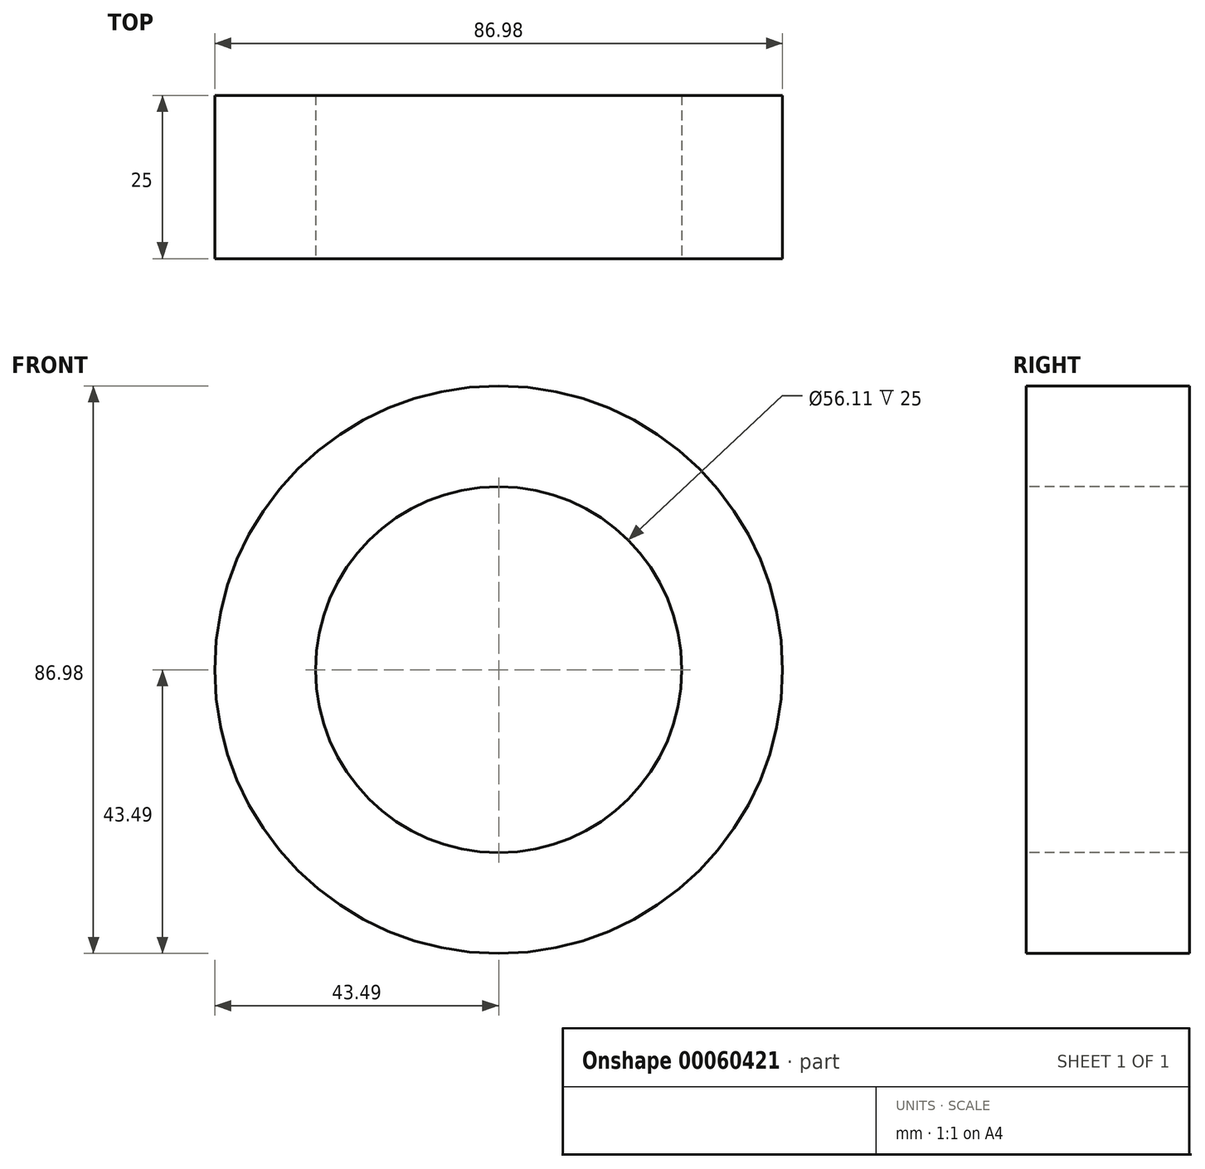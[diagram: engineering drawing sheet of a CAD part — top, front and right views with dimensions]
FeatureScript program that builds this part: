
annotation { "Feature Type Name" : "Feature", "Feature Type Description" : "" }
export const myFeature = defineFeature(function(context is Context, id is Id, definition is map)
    precondition{}
    {
        {
            var Q0;
            Q0=qCreatedBy(makeId("Front.planeOp"),FACE);
            var sketch = newSketch(context, id + "F0", { "sketchPlane" : qUnion([Q0])});
            skCircle(sketch, "E0", {"center": v(0, 0) * mm, "radius": 43.49 * mm});
            skCircle(sketch, "E1", {"center": v(0, 0) * mm, "radius": 28.05 * mm});
            skSolve(sketch);
        }
        {
            var Q0;
            Q0 = qSketchRegion(id + "F0", true);
            extrude(context, id + "F1", {"entities" : qUnion([Q0]), "depth" : 25 * mm, "hasDraft" : true, "draftAngle" : 0 * degree});
        }
    });
